# Revit family: 6252 11_Heizkörperanschluß mit Konus
name_source: partatom
category: Rohrformteile
units: mm (PartAtom-declared; Revit-internal decimal feet)

## family parameters
Arbeitsebenenbasiert = Nein
Beim Laden mit Abzugskörper schneiden = Nein
Bemaßung runder Anschluss = Durchmesser verwenden
Gemeinsam genutzt = Nein
Immer vertikal = Ja
OmniClass-Nummer = 23.65.55.14
OmniClass-Titel = Valves for Liquid Services
Teiletyp = Verbindung

## types (1)
- G3/4 x G1/2
    Anschlussstück = Messing CW614N, vernickelt
    Ausführung = Heizkörperanschluss mit freidrehender Überwurfmutter G3/4" und O-Ringdichtung.
    Bestellnummer = 1625211
    D00 = 17 mm
    D01 = 10 mm  [stored 0.0328084 ft]
    D02 = 11 mm
    D03 = 10 mm  [stored 0.0328084 ft]
    D04 = 8 mm  [stored 0.0262467 ft]
    GT = 9 mm  [stored 0.0295276 ft]
    Hersteller = HERZ Armaturen Ges.m.b.H.
    L00 = 25 mm  [stored 0.082021 ft]
    L01 = 13 mm
    L02 = 6 mm  [stored 0.019685 ft]
    L03 = 10 mm  [stored 0.0328084 ft]
    Max. Betriebsdruck = 1000000.0 Pa
    Max. Betriebstemperatur = 110 °C
    Medium = Heizungswasser nach ÖNORM H5195 oder VDI- Richtlinie 2035.
Die Verwendung von Ethylen- oder Propyleneglykol in einem Mischungsverhältnis 25- 50% ist zulässig.
    Mutter = Messing CW614N, vernickelt
    Nennweite_AG = 15 mm  [stored 0.0492126 ft]
    Nennweite_IG = 20 mm  [stored 0.0656168 ft]
    O-Ring = EPDM
    S01 = 9 mm  [stored 0.0295276 ft]
    S02 = 8 mm  [stored 0.0262467 ft]
    SCRNCODE = 07;01;02
    SCRNSEQ = AWI;AWI_TYP="1001";2
    URL = www.herz-armaturen.at
    Vorgabe-Ansicht = 0 mm  [stored 0 ft]

note: [stored X ft] marks values corroborated as IEEE doubles in the binary element streams (Revit-internal decimal feet)
